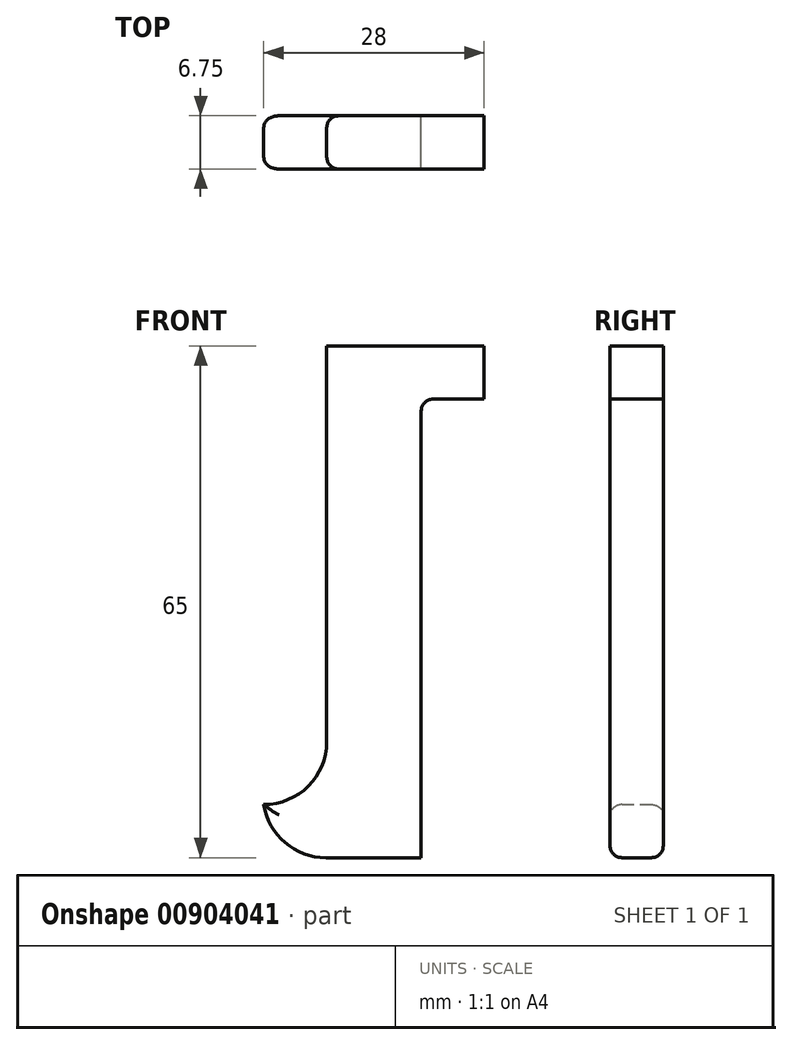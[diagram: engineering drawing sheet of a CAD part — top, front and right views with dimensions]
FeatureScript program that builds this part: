
annotation { "Feature Type Name" : "Feature", "Feature Type Description" : "" }
export const myFeature = defineFeature(function(context is Context, id is Id, definition is map)
    precondition{}
    {
        {
            var Q0;
            Q0=qCreatedBy(makeId("Front.planeOp"),FACE);
            var sketch = newSketch(context, id + "F0", { "sketchPlane" : qUnion([Q0])});
            skLineSegment(sketch, "E0.bottom", {"start": v(-102.62, 33.13) * mm, "end": v(-82.62, 33.13) * mm});
            skLineSegment(sketch, "E0.top", {"start": v(-90.62, 26.38) * mm, "end": v(-82.62, 26.38) * mm});
            skLineSegment(sketch, "E0.left", {"start": v(-102.62, 33.13) * mm, "end": v(-102.62, 26.38) * mm});
            skLineSegment(sketch, "E0.right", {"start": v(-82.62, 33.13) * mm, "end": v(-82.62, 26.38) * mm});
            skLineSegment(sketch, "E1.bottom", {"start": v(-102.62, 33.13) * mm, "end": v(-90.62, 33.13) * mm});
            skLineSegment(sketch, "E1.top", {"start": v(-102.62, -31.87) * mm, "end": v(-90.62, -31.87) * mm});
            skLineSegment(sketch, "E1.left", {"start": v(-102.62, 33.13) * mm, "end": v(-102.62, -25.12) * mm});
            skLineSegment(sketch, "E1.right", {"start": v(-90.62, 26.38) * mm, "end": v(-90.62, -31.87) * mm});
            skLineSegment(sketch, "E2.bottom", {"start": v(-90.62, -31.87) * mm, "end": v(-110.62, -31.87) * mm});
            skLineSegment(sketch, "E2.top", {"start": v(-102.62, -25.12) * mm, "end": v(-110.62, -25.12) * mm});
            skLineSegment(sketch, "E2.left", {"start": v(-90.62, -31.87) * mm, "end": v(-90.62, -25.12) * mm});
            skLineSegment(sketch, "E2.right", {"start": v(-110.62, -31.87) * mm, "end": v(-110.62, -25.12) * mm});
            skSolve(sketch);
        }
        {
            var Q0;
            {var subQ5=sQuery(id+"F0.wireOp",EDGE,"E2.right");Q0=makeQuery(id+"F0.imprint","IMPRINT",FACE,{"disambiguationData":[TD([[makeQuery(id+"F0.imprint","IMPRINT",EDGE,{"derivedFrom":subQ5}),-1.0]])]});}
            var Q1;
            {var subQ0=sQuery(id+"F0.wireOp",EDGE,"E0.bottom");Q1=makeQuery(id+"F0.imprint","IMPRINT",FACE,{"disambiguationData":[TD([[makeQuery(id+"F0.imprint","IMPRINT",EDGE,{"derivedFrom":subQ0}),-1.0]])]});}
            extrude(context, id + "F1", {"entities" : qUnion([Q0, Q1]), "depth" : 6.75 * mm, "offsetDistance" : 25 * mm});
        }
        {
            var Q0;
            Q0=makeQuery(id+"F1.opExtrude","SWEPT_EDGE",EDGE,{"disambiguationData":[OSD([sQuery(id+"F0.wireOp",EDGE,"E1.bottom"),sQuery(id+"F0.wireOp",EDGE,"E1.left")])]});
            var Q1;
            Q1=makeQuery(id+"F1.opExtrude","SWEPT_EDGE",EDGE,{"disambiguationData":[OSD([sQuery(id+"F0.wireOp",EDGE,"E2.bottom"),sQuery(id+"F0.wireOp",EDGE,"E2.left")])]});
            fillet(context, id + "F2", {"entities" : qUnion([Q0, Q1]), "radius" : 8 * mm, "tangentPropagation" : true, "defaultsChanged" : false, "vertexSettings" : [], "allowEdgeOverflow" : false});
        }
        {
            var Q0;
            Q0=makeQuery(id+"F1.opExtrude","CAP_EDGE",EDGE,{"disambiguationData":[OSD([sQuery(id+"F0.wireOp",EDGE,"E1.left")])],"isStart":true});
            var Q1;
            Q1=makeQuery(id+"F1.opExtrude","CAP_EDGE",EDGE,{"disambiguationData":[OSD([sQuery(id+"F0.wireOp",EDGE,"E2.top")])],"isStart":true});
            var Q2;
            Q2=makeQuery(id+"F1.opExtrude","CAP_EDGE",EDGE,{"disambiguationData":[OSD([sQuery(id+"F0.wireOp",EDGE,"E1.left")])],"isStart":false});
            var Q3;
            Q3=makeQuery(id+"F1.opExtrude","CAP_EDGE",EDGE,{"disambiguationData":[OSD([sQuery(id+"F0.wireOp",EDGE,"E2.top")])],"isStart":false});
            var Q4;
            Q4=makeQuery(id+"F1.opExtrude","SWEPT_EDGE",EDGE,{"disambiguationData":[OSD([sQuery(id+"F0.wireOp",EDGE,"E1.left"),sQuery(id+"F0.wireOp",EDGE,"E2.top")])]});
            var Q5;
            Q5=makeQuery(id+"F1.opExtrude","CAP_EDGE",EDGE,{"disambiguationData":[OSD([sQuery(id+"F0.wireOp",EDGE,"E2.bottom")])],"isStart":false});
            var Q6;
            Q6=makeQuery(id+"F1.opExtrude","CAP_EDGE",EDGE,{"disambiguationData":[OSD([sQuery(id+"F0.wireOp",EDGE,"E2.bottom")])],"isStart":true});
            var Q7;
            Q7=makeQuery(id+"F1.opExtrude","SWEPT_EDGE",EDGE,{"disambiguationData":[OSD([sQuery(id+"F0.wireOp",EDGE,"E0.top"),sQuery(id+"F0.wireOp",EDGE,"E1.right")])]});
            fillet(context, id + "F3", {"entities" : qUnion([Q0, Q1, Q2, Q3, Q4, Q5, Q6, Q7]), "radius" : 1.5 * mm, "tangentPropagation" : true, "defaultsChanged" : false, "vertexSettings" : [], "allowEdgeOverflow" : false});
        }
    });
